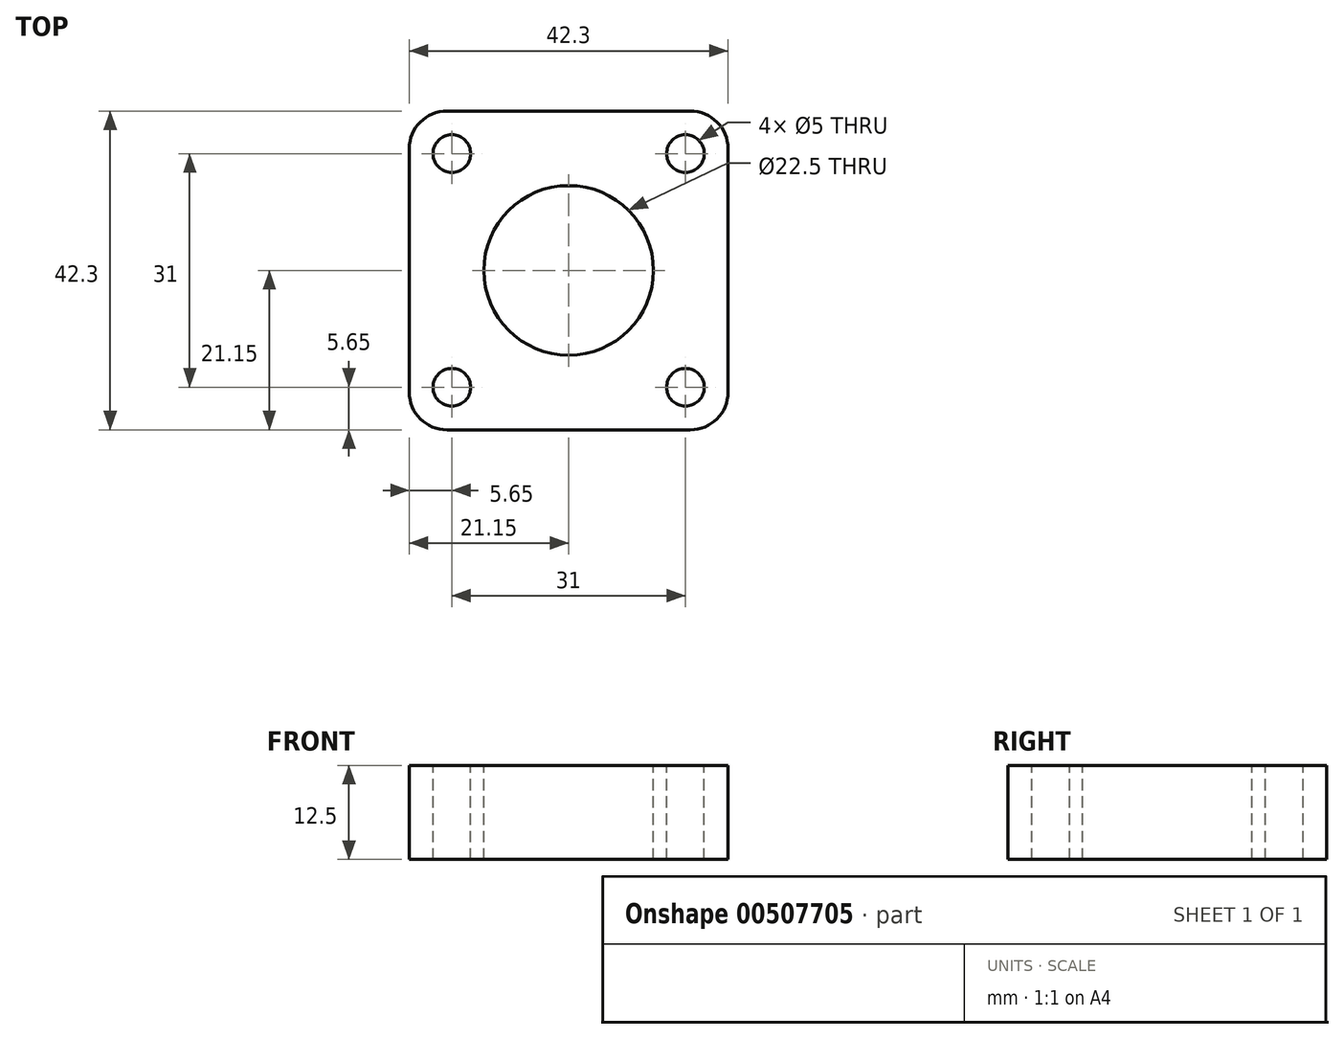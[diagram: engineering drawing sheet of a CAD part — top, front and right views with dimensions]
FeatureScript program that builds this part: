
annotation { "Feature Type Name" : "Feature", "Feature Type Description" : "" }
export const myFeature = defineFeature(function(context is Context, id is Id, definition is map)
    precondition{}
    {
        {
            var Q0;
            Q0=qCreatedBy(makeId("Top.planeOp"),FACE);
            var sketch = newSketch(context, id + "F0", { "sketchPlane" : qUnion([Q0])});
            skLineSegment(sketch, "E0.bottom", {"start": v(-21.15, 21.15) * mm, "end": v(21.15, 21.15) * mm});
            skLineSegment(sketch, "E0.top", {"start": v(-21.15, -21.15) * mm, "end": v(21.15, -21.15) * mm});
            skLineSegment(sketch, "E0.left", {"start": v(-21.15, 21.15) * mm, "end": v(-21.15, -21.15) * mm});
            skLineSegment(sketch, "E0.right", {"start": v(21.15, 21.15) * mm, "end": v(21.15, -21.15) * mm});
            skPoint(sketch, "E0.middle", {"position": v(0, 0) * mm});
            skLineSegment(sketch, "E1.bottom", {"start": v(-15.5, 15.5) * mm, "end": v(15.5, 15.5) * mm});
            skLineSegment(sketch, "E1.top", {"start": v(-15.5, -15.5) * mm, "end": v(15.5, -15.5) * mm});
            skLineSegment(sketch, "E1.left", {"start": v(-15.5, 15.5) * mm, "end": v(-15.5, -15.5) * mm});
            skLineSegment(sketch, "E1.right", {"start": v(15.5, 15.5) * mm, "end": v(15.5, -15.5) * mm});
            skCircle(sketch, "E2", {"center": v(0, 0) * mm, "radius": 11.25 * mm});
            skSolve(sketch);
        }
        {
            var Q0;
            Q0=makeQuery(id+"F0.imprint","IMPRINT",FACE,{"disambiguationData":[TD([[makeQuery(id+"F0.imprint","IMPRINT",EDGE,{"derivedFrom":sQuery(id+"F0.wireOp",EDGE,"E0.bottom")}),-1.0]])]});
            var Q1;
            Q1=makeQuery(id+"F0.imprint","IMPRINT",FACE,{"disambiguationData":[TD([[makeQuery(id+"F0.imprint","IMPRINT",EDGE,{"derivedFrom":sQuery(id+"F0.wireOp",EDGE,"E1.bottom")}),-1.0]])]});
            extrude(context, id + "F1", {"entities" : qUnion([Q0, Q1]), "oppositeDirection" : true, "depth" : 12.5 * mm});
        }
        {
            var Q0;
            Q0=makeQuery(id+"F1.opExtrude","SWEPT_EDGE",EDGE,{"disambiguationData":[OSD([sQuery(id+"F0.wireOp",EDGE,"E0.top"),sQuery(id+"F0.wireOp",EDGE,"E0.right")])]});
            var Q1;
            Q1=makeQuery(id+"F1.opExtrude","SWEPT_EDGE",EDGE,{"disambiguationData":[OSD([sQuery(id+"F0.wireOp",EDGE,"E0.bottom"),sQuery(id+"F0.wireOp",EDGE,"E0.left")])]});
            var Q2;
            Q2=makeQuery(id+"F1.opExtrude","SWEPT_EDGE",EDGE,{"disambiguationData":[OSD([sQuery(id+"F0.wireOp",EDGE,"E0.bottom"),sQuery(id+"F0.wireOp",EDGE,"E0.right")])]});
            fillet(context, id + "F2", {"entities" : qUnion([Q0, Q1, Q2]), "radius" : 5 * mm, "tangentPropagation" : true, "allowEdgeOverflow" : false});
        }
        {
            var Q0;
            Q0=makeQuery(id+"F1.opExtrude","SWEPT_EDGE",EDGE,{"disambiguationData":[OSD([sQuery(id+"F0.wireOp",EDGE,"E0.top"),sQuery(id+"F0.wireOp",EDGE,"E0.left")])]});
            fillet(context, id + "F3", {"entities" : qUnion([Q0]), "radius" : 5 * mm, "tangentPropagation" : true, "allowEdgeOverflow" : false});
        }
        {
            var Q0;
            Q0=sQuery(id+"F0.wireOp",VERTEX,"E1.top.start");
            var Q1;
            Q1=sQuery(id+"F0.wireOp",VERTEX,"E1.left.start");
            var Q2;
            Q2=sQuery(id+"F0.wireOp",VERTEX,"E1.bottom.end");
            var Q3;
            Q3=sQuery(id+"F0.wireOp",VERTEX,"E1.top.end");
            var Q4;
            Q4=makeQuery(id+"F1.opExtrude","SWEPT_BODY",BODY,{"disambiguationData":[OSD([sQuery(id+"F0.wireOp",EDGE,"E0.bottom"),sQuery(id+"F0.wireOp",EDGE,"E0.top"),sQuery(id+"F0.wireOp",EDGE,"E0.left"),sQuery(id+"F0.wireOp",EDGE,"E0.right"),sQuery(id+"F0.wireOp",EDGE,"E2")])]});
            hole(context, id + "F4", {"style" : HoleStyle.SIMPLE, "endStyle" : HoleEndStyle.THROUGH, "holeDiameter" : 5 * mm, "isTappedThrough" : true, "tappedDepth" : 12 * mm, "tapClearance" : 3, "locations" : qUnion([Q0, Q1, Q2, Q3]), "scope" : qUnion([Q4])});
        }
    });
